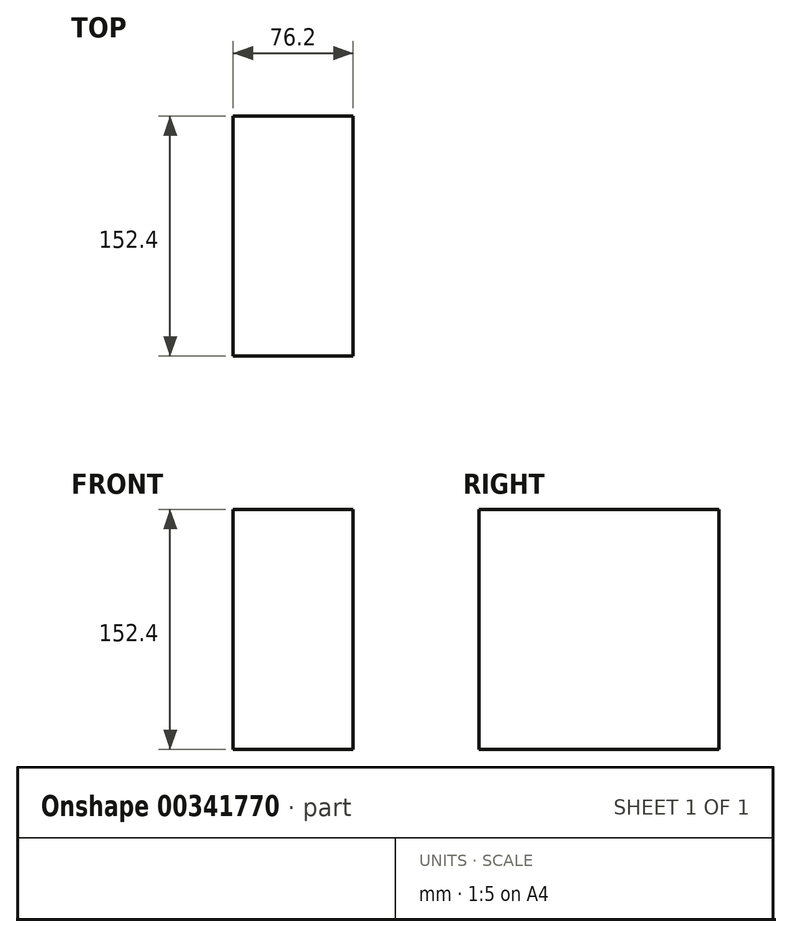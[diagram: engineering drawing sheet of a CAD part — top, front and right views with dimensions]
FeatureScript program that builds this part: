
annotation { "Feature Type Name" : "Feature", "Feature Type Description" : "" }
export const myFeature = defineFeature(function(context is Context, id is Id, definition is map)
    precondition{}
    {
        {
            var Q0;
            Q0=qCreatedBy(makeId("Front.planeOp"),FACE);
            var sketch = newSketch(context, id + "F0", { "sketchPlane" : qUnion([Q0])});
            skLineSegment(sketch, "E0.bottom", {"start": v(0, 0) * mm, "end": v(76.2, 0) * mm});
            skLineSegment(sketch, "E0.top", {"start": v(0, 152.4) * mm, "end": v(76.2, 152.4) * mm});
            skLineSegment(sketch, "E0.left", {"start": v(0, 0) * mm, "end": v(0, 152.4) * mm});
            skLineSegment(sketch, "E0.right", {"start": v(76.2, 0) * mm, "end": v(76.2, 152.4) * mm});
            skSolve(sketch);
        }
        {
            var Q0;
            Q0 = qSketchRegion(id + "F0", true);
            extrude(context, id + "F1", {"entities" : qUnion([Q0]), "depth" : 152.4 * mm});
        }
    });
